# Revit family: 10.0kW-14.0kW
name_source: partatom
category: Mechanical Equipment
revit_build: Autodesk Revit 2013 (Build: 20120221_2030(x64)
units: mm (PartAtom-declared; Revit-internal decimal feet)

## types (4) — shared parameters
Condensation = Air
Depth = 674 mm  [stored 2.21129 ft]
Description = High efficiency air cooled
Gas = R32/R410A
Gas pipe = 15.9 mm  [stored 0.0521654 ft]
Gas pipe radius = 7.95 mm  [stored 0.0260827 ft]
Height = 234 mm  [stored 0.767717 ft]
Installation = Indoor installation
Liquid pipe = 9.52 mm
Liquid pipe radius = 4.76 mm
MCA (Minimum Circuit Amps) = 1 A
MFA (Maximum Fuse Amps) = 15 A
Machine material = Galvanized Steel
Net Weight = 36.40 kg
Panel color = S1004
Power supply = 1-phase, 220-240V, 50Hz
Series = VRF
Width = 1649 mm
drain pipe = 25 mm  [stored 0.082021 ft]
drain pipe radius = 12.5 mm  [stored 0.0410105 ft]

## per-type parameters (varying)
| type | Air  Flow | Cooling Capacity | Cooling Power Input | Heating Capacity | Heating Power Input |
| 10.0kW | 1497/1469/1296/1200/1104/1015/918 m3/h | 10 kW | 50 W | 11 kW | 50 W |
| 11.2kW | 1648/1530/1469/1292/1178/1067/956 m3/h | 11 kW | 65 W | 13 kW | 65 W |
| 12.5kW | 2012/1879/1772/1649/1531/1469/1285 m3/h | 13 kW | 95 W | 14 kW | 95 W |
| 14.0kW | 2206/2070/1937/1810/1677/1516/1402 m3/h | 14 kW | 140 W | 16 kW | 140 W |

note: [stored X ft] marks values corroborated as IEEE doubles in the binary element streams (Revit-internal decimal feet)
